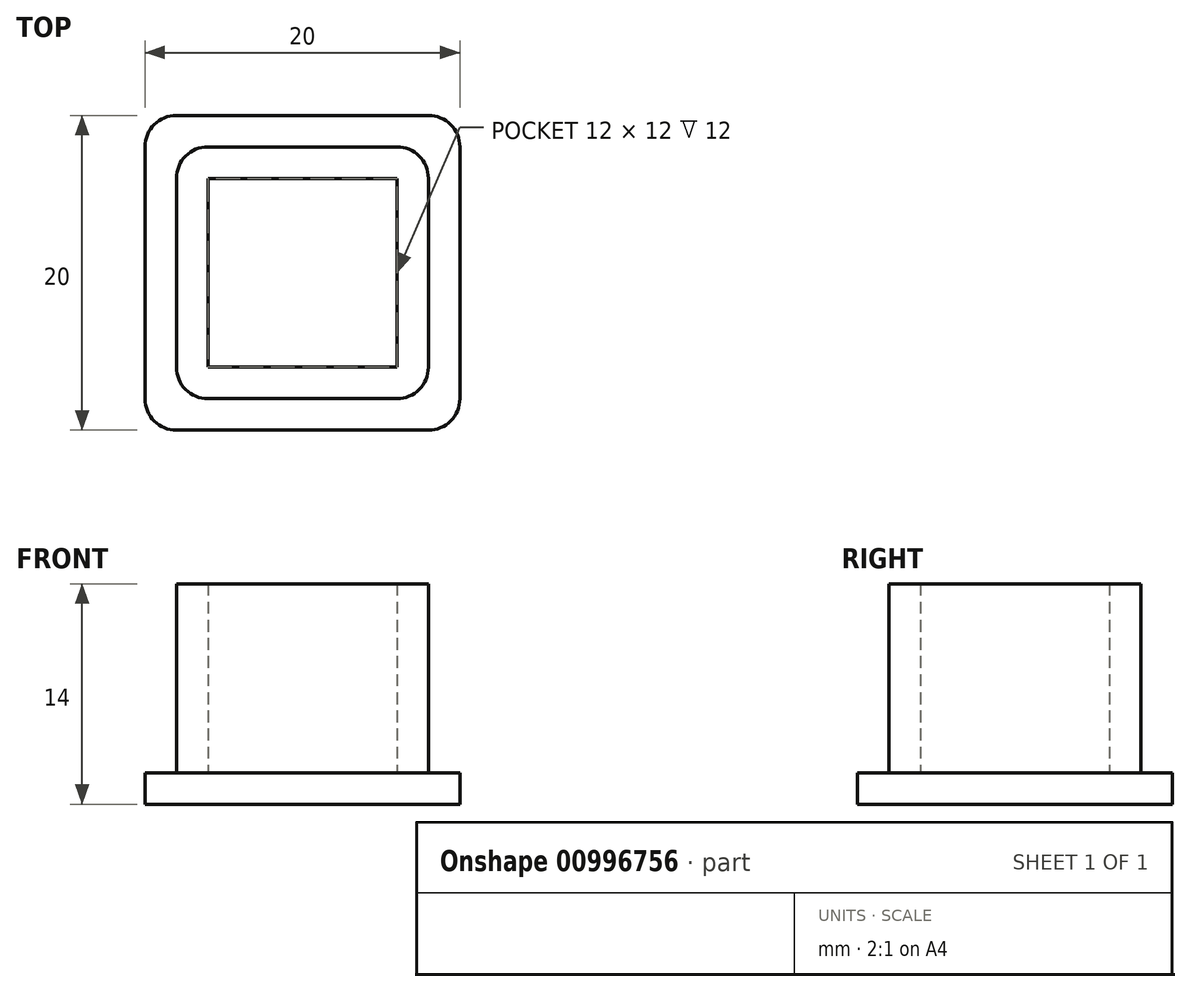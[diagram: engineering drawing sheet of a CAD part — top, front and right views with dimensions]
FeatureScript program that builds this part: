
annotation { "Feature Type Name" : "Feature", "Feature Type Description" : "" }
export const myFeature = defineFeature(function(context is Context, id is Id, definition is map)
    precondition{}
    {
        {
            var Q0;
            Q0=qCreatedBy(makeId("Top.planeOp"),FACE);
            var sketch = newSketch(context, id + "F0", { "sketchPlane" : qUnion([Q0])});
            skLineSegment(sketch, "E0.bottom", {"start": v(10, -10) * mm, "end": v(-10, -10) * mm});
            skLineSegment(sketch, "E0.top", {"start": v(10, 10) * mm, "end": v(-10, 10) * mm});
            skLineSegment(sketch, "E0.left", {"start": v(10, -10) * mm, "end": v(10, 10) * mm});
            skLineSegment(sketch, "E0.right", {"start": v(-10, -10) * mm, "end": v(-10, 10) * mm});
            skPoint(sketch, "E0.middle", {"position": v(0, 0) * mm});
            skSolve(sketch);
        }
        {
            var Q0;
            Q0=makeQuery(id+"F0.imprint","IMPRINT",FACE,{"disambiguationData":[TD([[makeQuery(id+"F0.imprint","IMPRINT",EDGE,{"derivedFrom":sQuery(id+"F0.wireOp",EDGE,"E0.bottom")}),-1.0]])]});
            extrude(context, id + "F1", {"entities" : qUnion([Q0]), "depth" : 2 * mm, "offsetDistance" : 25 * mm});
        }
        {
            var Q0;
            Q0=makeQuery(id+"F1.opExtrude","CAP_FACE",FACE,{"disambiguationData":[OSD([sQuery(id+"F0.wireOp",EDGE,"E0.bottom"),sQuery(id+"F0.wireOp",EDGE,"E0.top"),sQuery(id+"F0.wireOp",EDGE,"E0.left"),sQuery(id+"F0.wireOp",EDGE,"E0.right")])],"isStart":false});
            var sketch = newSketch(context, id + "F2", { "sketchPlane" : qUnion([Q0])});
            skLineSegment(sketch, "E1.bottom", {"start": v(-8, -8) * mm, "end": v(8, -8) * mm});
            skLineSegment(sketch, "E1.top", {"start": v(-8, 8) * mm, "end": v(8, 8) * mm});
            skLineSegment(sketch, "E1.left", {"start": v(-8, -8) * mm, "end": v(-8, 8) * mm});
            skLineSegment(sketch, "E1.right", {"start": v(8, -8) * mm, "end": v(8, 8) * mm});
            skPoint(sketch, "E1.middle", {"position": v(0, 0) * mm});
            skLineSegment(sketch, "E2.bottom", {"start": v(-6, -6) * mm, "end": v(6, -6) * mm});
            skLineSegment(sketch, "E2.top", {"start": v(-6, 6) * mm, "end": v(6, 6) * mm});
            skLineSegment(sketch, "E2.left", {"start": v(-6, -6) * mm, "end": v(-6, 6) * mm});
            skLineSegment(sketch, "E2.right", {"start": v(6, -6) * mm, "end": v(6, 6) * mm});
            skLineSegment(sketch, "E3", {"start": v(0.97, 8) * mm, "end": v(0.97, 10) * mm, "construction": true});
            skLineSegment(sketch, "E4", {"start": v(8, 1.78) * mm, "end": v(10, 1.78) * mm, "construction": true});
            skPoint(sketch, "E4.endSnap0", {"position": v(10, 0) * mm});
            skSolve(sketch);
        }
        {
            var Q0;
            Q0=makeQuery(id+"F2.imprint","IMPRINT",FACE,{"disambiguationData":[TD([[makeQuery(id+"F2.imprint","IMPRINT",EDGE,{"derivedFrom":sQuery(id+"F2.wireOp",EDGE,"E1.bottom")}),1.0]])]});
            extrude(context, id + "F3", {"entities" : qUnion([Q0]), "operationType" : NewBodyOperationType.ADD, "depth" : 12 * mm, "offsetDistance" : 25 * mm});
        }
        {
            var Q0;
            Q0=makeQuery(id+"F1.opExtrude","SWEPT_EDGE",EDGE,{"disambiguationData":[OSD([sQuery(id+"F0.wireOp",EDGE,"E0.top"),sQuery(id+"F0.wireOp",EDGE,"E0.right")])]});
            var Q1;
            Q1=makeQuery(id+"F3.opExtrude","SWEPT_EDGE",EDGE,{"disambiguationData":[OSD([sQuery(id+"F2.wireOp",EDGE,"E1.top"),sQuery(id+"F2.wireOp",EDGE,"E1.left")])]});
            var Q2;
            Q2=makeQuery(id+"F1.opExtrude","SWEPT_EDGE",EDGE,{"disambiguationData":[OSD([sQuery(id+"F0.wireOp",EDGE,"E0.bottom"),sQuery(id+"F0.wireOp",EDGE,"E0.right")])]});
            var Q3;
            Q3=makeQuery(id+"F3.opExtrude","SWEPT_EDGE",EDGE,{"disambiguationData":[OSD([sQuery(id+"F2.wireOp",EDGE,"E1.bottom"),sQuery(id+"F2.wireOp",EDGE,"E1.left")])]});
            var Q4;
            Q4=makeQuery(id+"F1.opExtrude","SWEPT_EDGE",EDGE,{"disambiguationData":[OSD([sQuery(id+"F0.wireOp",EDGE,"E0.top"),sQuery(id+"F0.wireOp",EDGE,"E0.left")])]});
            var Q5;
            Q5=makeQuery(id+"F3.opExtrude","SWEPT_EDGE",EDGE,{"disambiguationData":[OSD([sQuery(id+"F2.wireOp",EDGE,"E1.top"),sQuery(id+"F2.wireOp",EDGE,"E1.right")])]});
            var Q6;
            Q6=makeQuery(id+"F1.opExtrude","SWEPT_EDGE",EDGE,{"disambiguationData":[OSD([sQuery(id+"F0.wireOp",EDGE,"E0.bottom"),sQuery(id+"F0.wireOp",EDGE,"E0.left")])]});
            var Q7;
            Q7=makeQuery(id+"F3.opExtrude","SWEPT_EDGE",EDGE,{"disambiguationData":[OSD([sQuery(id+"F2.wireOp",EDGE,"E1.bottom"),sQuery(id+"F2.wireOp",EDGE,"E1.right")])]});
            fillet(context, id + "F4", {"entities" : qUnion([Q0, Q1, Q2, Q3, Q4, Q5, Q6, Q7]), "radius" : 2 * mm, "tangentPropagation" : true, "allowEdgeOverflow" : false});
        }
    });
